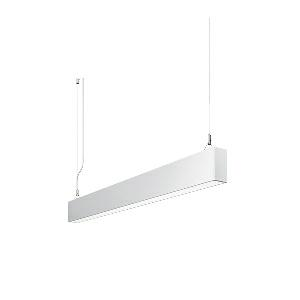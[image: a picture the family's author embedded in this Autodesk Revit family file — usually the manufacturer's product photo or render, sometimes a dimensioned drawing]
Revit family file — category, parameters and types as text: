
# Revit family: idoo_line_-_ilp_2000_vtl_d_00806414_bcd3
name_source: partatom
category: Lighting Fixtures
units: mm (PartAtom-declared; Revit-internal decimal feet)

## family parameters
Cut with Voids When Loaded = No
Host = Face
Light Source = No
Part Type = Normal
Room Calculation Point = No
Round Connector Dimension = Use Diameter
Shared = No

## types (1)
- IDOO.line - ILP 2000/VTL/D (1 x LED, 2300 lm, 2700-6500K)
    Apparent Load = 23 VA
    Approval mark = CE
    CIE Flux Codes = 66 91 98 40 100
    Color Rendering = 90-100
    Color Temperature = 2700-6500K
    Control Gear = Electronic ballast
    Default Elevation = 1800 mm
    Description = ILP 2000/VTL/D|Suspended luminaire|light source: LED|connected load: 220-240 V, 50/60 Hz|Power consumption: approx. 23 W|standby: approx. 0,25|luminous flux: 2300 lm|luminous efficacy: 100 lm/W|light distribution: Direct/indirect|direct ratio: approx. 40 %|colour temperature: Cold white, ca. 2700-6500 K|color rendering index (CRI): >= 90|chromaticity tolerance:  3 SDCM|System of protection: IP 40|technology: Continuously dimmable|luminaire body|material: Sectional aluminium|colour: White|lamp cover: Plastic, Structured|mains lead: 2.00 m With free stranded wires|Fastening: Steel cable 0.3 - 0.7 m|glare control: Prism aperture|luminance(L65): <= 2700 cd/m|unified glare rating(4H 8H): <=  16|special features: Specified values at approx. 4000 K, DALI Load 1x, External control required for Dali Device type 8, Flicker-free, Constant luminous flux between 2700 and 6500 K, Constant colour temperature over the whole dimming range, Suitable as emergency lighting|
    Frequency = 50 Hz
    Height = 110 mm
    Lamp = 1 x LED
    Lamp Light Flux = 2300 lm
    Lamp count = 1
    Length = 854 mm
    Luminous efficacy = 100 lm/W
    Manufacturer = Waldmann
    ModVariant = No
    Model = 00806414
    Mounting Place = Ceiling
    Mounting Type = Pendant
    Number of Poles = 1
    OnlyDefault = Yes
    Power Factor = 1
    Product Name = IDOO.line - ILP 2000/VTL/D
    Product group = Suspended luminaire
    ProductGroupID = 9
    Protection Class = Protection class I
    Protection Degree = IP 40
    RLX_Detail_Level = 1
    RLX_Emergency_Light_Flux = 0 lm
    RLX_Emergency_Type = 0
    RLX_Emergency_Type_DB = No
    RlxData = <blob elided: 17913 chars, md5=a824bf25>
    Socket = socket
    Standby Power = 0 W
    System Light Flux = 2300 lm
    System Power = 23 W
    Type Comments = Product without accessories
    Type Image = 113287000-00692509.jpg
    URL = http://relux.com
    VarID = ---
    Voltage = 230 V
    Voltage Range = 220-240 V
    Weight = 0.00 kg
    Width = 60 mm  [stored 0.19685 ft]

note: [stored X ft] marks values corroborated as IEEE doubles in the binary element streams (Revit-internal decimal feet)

## geometry (parser evidence)
native form markers: Blend x4, Sweep x13
no freeform markers — native parametric forms only
